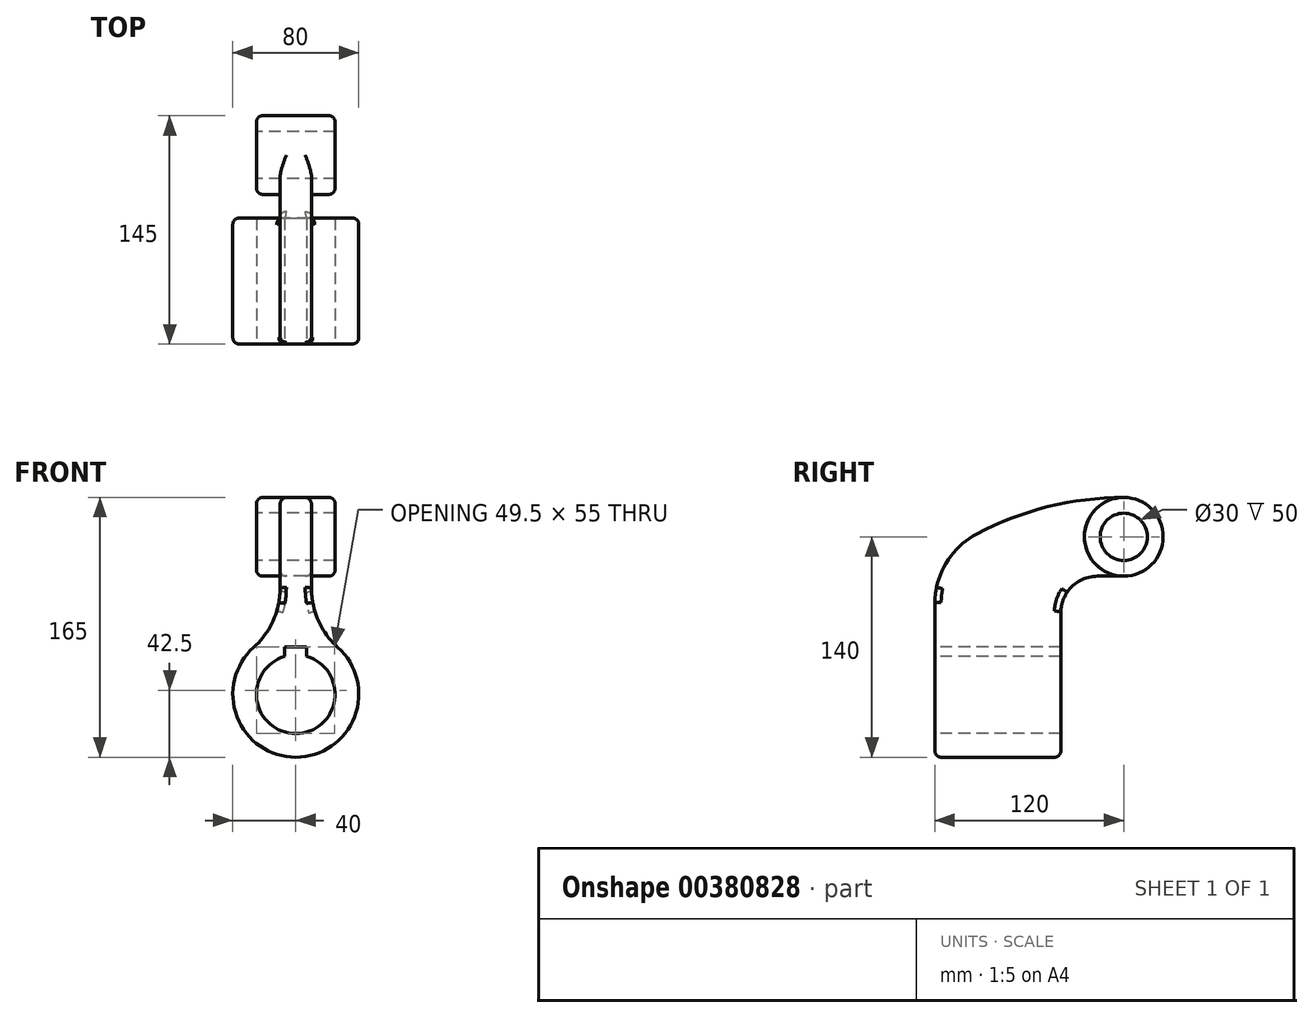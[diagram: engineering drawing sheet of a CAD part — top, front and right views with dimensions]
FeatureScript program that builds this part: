
annotation { "Feature Type Name" : "Feature", "Feature Type Description" : "" }
export const myFeature = defineFeature(function(context is Context, id is Id, definition is map)
    precondition{}
    {
        {
            var Q0;
            Q0=qCreatedBy(makeId("Right.planeOp"),FACE);
            var sketch = newSketch(context, id + "F0", { "sketchPlane" : qUnion([Q0])});
            skLineSegment(sketch, "E0.bottom", {"start": v(80, 25) * mm, "end": v(0, 25) * mm});
            skLineSegment(sketch, "E0.top", {"start": v(80, 40) * mm, "end": v(0, 40) * mm});
            skLineSegment(sketch, "E0.left", {"start": v(80, 25) * mm, "end": v(80, 40) * mm});
            skLineSegment(sketch, "E0.right", {"start": v(0, 25) * mm, "end": v(0, 40) * mm});
            skLineSegment(sketch, "E1", {"start": v(0, 0) * mm, "end": v(81.16, 0) * mm, "construction": true});
            skLineSegment(sketch, "E2", {"start": v(0, 40) * mm, "end": v(0, 57.66) * mm});
            skArc(sketch, "E3", {"start": v(0, 57.66) * mm, "mid": v(7.18, 83.48) * mm, "end": v(26.67, 101.89) * mm});
            skArc(sketch, "E4", {"start": v(26.67, 101.89) * mm, "mid": v(71.92, 119.14) * mm, "end": v(120, 125) * mm});
            skCircle(sketch, "E5", {"center": v(120, 100) * mm, "radius": 25 * mm});
            skPoint(sketch, "E5.second.point", {"position": v(120, 75) * mm});
            skCircle(sketch, "E6", {"center": v(120, 100) * mm, "radius": 15 * mm});
            skLineSegment(sketch, "E7", {"start": v(80, 40) * mm, "end": v(80, 51.7) * mm});
            skLineSegment(sketch, "E8", {"start": v(120, 75) * mm, "end": v(103.3, 75) * mm});
            skArc(sketch, "E9", {"start": v(80, 51.7) * mm, "mid": v(86.82, 68.18) * mm, "end": v(103.3, 75) * mm});
            skSolve(sketch);
        }
        {
            var Q0;
            Q0=makeQuery(id+"F0.imprint","IMPRINT",FACE,{"disambiguationData":[TD([[makeQuery(id+"F0.imprint","IMPRINT",EDGE,{"derivedFrom":sQuery(id+"F0.wireOp",EDGE,"E0.bottom")}),-1.0]])]});
            var Q1;
            Q1=sQuery(id+"F0.wireOp",EDGE,"E1");
            revolve(context, id + "F1", {"entities" : qUnion([Q0]), "axis" : qUnion([Q1]), "revolveType" : RevolveType.FULL});
        }
        {
            var Q0;
            Q0=makeQuery(id+"F0.imprint","IMPRINT",FACE,{"disambiguationData":[TD([[makeQuery(id+"F0.imprint","IMPRINT",EDGE,{"derivedFrom":sQuery(id+"F0.wireOp",EDGE,"E0.top")}),-1.0]])]});
            var Q1;
            Q1=makeQuery(id+"F0.imprint","IMPRINT",FACE,{"disambiguationData":[TD([[makeQuery(id+"F0.imprint","IMPRINT",EDGE,{"derivedFrom":sQuery(id+"F0.wireOp",EDGE,"E0.bottom")}),-1.0]])]});
            extrude(context, id + "F2", {"entities" : qUnion([Q0, Q1]), "operationType" : NewBodyOperationType.ADD, "endBound" : BoundingType.SYMMETRIC, "depth" : 20 * mm});
        }
        {
            var Q0;
            {var subQ0=sQuery(id+"F0.wireOp",EDGE,"E5");var subQ1=makeQuery(id+"F0.imprint","INTERSECT",VERTEX,{"derivedFrom":[sQuery(id+"F0.wireOp",EDGE,"E4"),subQ0]});Q0=makeQuery(id+"F0.imprint","IMPRINT",FACE,{"disambiguationData":[TD([[makeQuery(id+"F0.imprint","IMPRINT",EDGE,{"disambiguationData":[TD([[subQ1,-1.0]])],"derivedFrom":subQ0}),1.0]])]});}
            extrude(context, id + "F3", {"entities" : qUnion([Q0]), "operationType" : NewBodyOperationType.ADD, "endBound" : BoundingType.SYMMETRIC, "depth" : 50 * mm});
        }
        {
            var Q0;
            Q0=makeQuery(id+"F2.boolean.opBoolean","INTERSECT",EDGE,{"derivedFrom":[makeQuery(id+"F1.opRevolve","SWEPT_FACE",FACE,{"disambiguationData":[OSD([sQuery(id+"F0.wireOp",EDGE,"E0.top")])]}),makeQuery(id+"F2.opExtrude","CAP_FACE",FACE,{"disambiguationData":[OSD([sQuery(id+"F0.wireOp",EDGE,"E0.bottom"),sQuery(id+"F0.wireOp",EDGE,"E0.left"),sQuery(id+"F0.wireOp",EDGE,"E0.right"),sQuery(id+"F0.wireOp",EDGE,"E2"),sQuery(id+"F0.wireOp",EDGE,"E3"),sQuery(id+"F0.wireOp",EDGE,"E4"),sQuery(id+"F0.wireOp",EDGE,"E5"),sQuery(id+"F0.wireOp",EDGE,"E7"),sQuery(id+"F0.wireOp",EDGE,"E8"),sQuery(id+"F0.wireOp",EDGE,"E9")])],"isStart":false})]});
            var Q1;
            Q1=makeQuery(id+"F2.boolean.opBoolean","INTERSECT",EDGE,{"derivedFrom":[makeQuery(id+"F1.opRevolve","SWEPT_FACE",FACE,{"disambiguationData":[OSD([sQuery(id+"F0.wireOp",EDGE,"E0.top")])]}),makeQuery(id+"F2.opExtrude","CAP_FACE",FACE,{"disambiguationData":[OSD([sQuery(id+"F0.wireOp",EDGE,"E0.bottom"),sQuery(id+"F0.wireOp",EDGE,"E0.left"),sQuery(id+"F0.wireOp",EDGE,"E0.right"),sQuery(id+"F0.wireOp",EDGE,"E2"),sQuery(id+"F0.wireOp",EDGE,"E3"),sQuery(id+"F0.wireOp",EDGE,"E4"),sQuery(id+"F0.wireOp",EDGE,"E5"),sQuery(id+"F0.wireOp",EDGE,"E7"),sQuery(id+"F0.wireOp",EDGE,"E8"),sQuery(id+"F0.wireOp",EDGE,"E9")])],"isStart":true})]});
            fillet(context, id + "F4", {"entities" : qUnion([Q0, Q1]), "radius" : 50 * mm, "tangentPropagation" : true, "allowEdgeOverflow" : false});
        }
        {
            var Q0;
            Q0=makeQuery(id+"F2.opExtrude","CAP_EDGE",EDGE,{"disambiguationData":[OSD([sQuery(id+"F0.wireOp",EDGE,"E5")])],"isStart":false});
            var Q1;
            Q1=makeQuery(id+"F2.opExtrude","CAP_EDGE",EDGE,{"disambiguationData":[OSD([sQuery(id+"F0.wireOp",EDGE,"E5")])],"isStart":true});
            var Q2;
            Q2=makeQuery(id+"F1.opRevolve","SWEPT_EDGE",EDGE,{"disambiguationData":[OSD([sQuery(id+"F0.wireOp",EDGE,"E0.top"),sQuery(id+"F0.wireOp",EDGE,"E0.right"),sQuery(id+"F0.wireOp",EDGE,"E2")])]});
            var Q3;
            Q3=makeQuery(id+"F3.opExtrude","CAP_EDGE",EDGE,{"disambiguationData":[OSD([sQuery(id+"F0.wireOp",EDGE,"E5")])],"isStart":true});
            var Q4;
            Q4=makeQuery(id+"F3.opExtrude","CAP_EDGE",EDGE,{"disambiguationData":[OSD([sQuery(id+"F0.wireOp",EDGE,"E5")])],"isStart":false});
            fillet(context, id + "F5", {"entities" : qUnion([Q0, Q1, Q2, Q3, Q4]), "radius" : 4 * mm, "tangentPropagation" : true, "allowEdgeOverflow" : false});
        }
        {
            var Q0;
            Q0=makeQuery(id+"F1.opRevolve","SWEPT_EDGE",EDGE,{"disambiguationData":[OSD([sQuery(id+"F0.wireOp",EDGE,"E0.top"),sQuery(id+"F0.wireOp",EDGE,"E0.left"),sQuery(id+"F0.wireOp",EDGE,"E7")])]});
            fillet(context, id + "F6", {"entities" : qUnion([Q0]), "radius" : 4 * mm, "tangentPropagation" : true, "allowEdgeOverflow" : false});
        }
        {
            var Q0;
            {var subQ0=sQuery(id+"F0.wireOp",EDGE,"E0.right");Q0=makeQuery(id+"F2.boolean.opBoolean","MERGE",FACE,{"derivedFrom":[makeQuery(id+"F1.opRevolve","SWEPT_FACE",FACE,{"disambiguationData":[OSD([subQ0])]}),makeQuery(id+"F2.opExtrude","SWEPT_FACE",FACE,{"disambiguationData":[OSD([subQ0,sQuery(id+"F0.wireOp",EDGE,"E2")])]})]});}
            var sketch = newSketch(context, id + "F7", { "sketchPlane" : qUnion([Q0])});
            skLineSegment(sketch, "E10.bottom", {"start": v(7, 30) * mm, "end": v(-7, 30) * mm});
            skLineSegment(sketch, "E10.top", {"start": v(7, 24) * mm, "end": v(-7, 24) * mm});
            skLineSegment(sketch, "E10.left", {"start": v(7, 30) * mm, "end": v(7, 24) * mm});
            skLineSegment(sketch, "E10.right", {"start": v(-7, 30) * mm, "end": v(-7, 24) * mm});
            skLineSegment(sketch, "E11", {"start": v(0, -25) * mm, "end": v(-61.56, -25) * mm, "construction": true});
            skSolve(sketch);
        }
        {
            var Q0;
            Q0 = qSketchRegion(id + "F7", true);
            extrude(context, id + "F8", {"entities" : qUnion([Q0]), "operationType" : NewBodyOperationType.REMOVE, "endBound" : BoundingType.UP_TO_NEXT, "oppositeDirection" : true, "depth" : 25 * mm});
        }
    });
